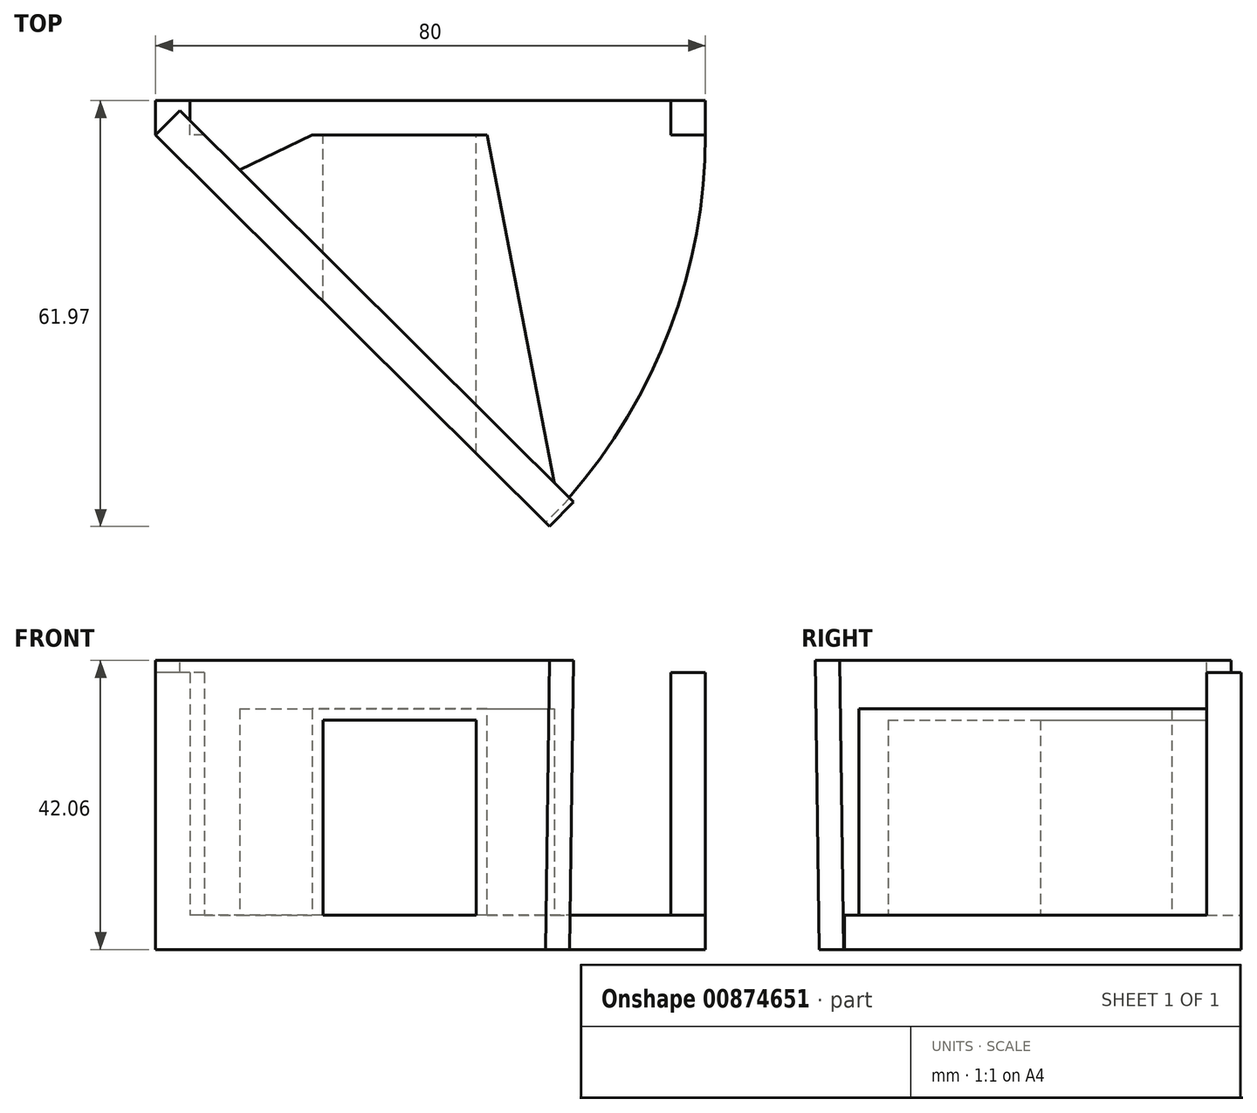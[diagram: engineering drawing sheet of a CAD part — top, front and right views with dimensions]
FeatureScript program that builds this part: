
annotation { "Feature Type Name" : "Feature", "Feature Type Description" : "" }
export const myFeature = defineFeature(function(context is Context, id is Id, definition is map)
    precondition{}
    {
        {
            var Q0;
            Q0=qCreatedBy(makeId("Front.planeOp"),FACE);
            var sketch = newSketch(context, id + "F0", { "sketchPlane" : qUnion([Q0])});
            skLineSegment(sketch, "E0.bottom", {"start": v(0, 0) * mm, "end": v(-80, 0) * mm});
            skLineSegment(sketch, "E0.top", {"start": v(0, 40.27) * mm, "end": v(-80, 40.27) * mm});
            skLineSegment(sketch, "E0.left", {"start": v(0, 0) * mm, "end": v(0, 40.27) * mm});
            skLineSegment(sketch, "E0.right", {"start": v(-80, 0) * mm, "end": v(-80, 40.27) * mm});
            skSolve(sketch);
        }
        {
            var Q0;
            Q0 = qSketchRegion(id + "F0", true);
            extrude(context, id + "F1", {"entities" : qUnion([Q0]), "depth" : 5 * mm, "offsetDistance" : 25 * mm});
        }
        {
            var Q0;
            Q0=qCreatedBy(makeId("Top.planeOp"),FACE);
            var sketch = newSketch(context, id + "F2", { "sketchPlane" : qUnion([Q0])});
            skLineSegment(sketch, "E1", {"start": v(0, -4.77) * mm, "end": v(-80, -5) * mm});
            skArc(sketch, "E2", {"start": v(0, -4.77) * mm, "mid": v(-6, -35.4) * mm, "end": v(-23.27, -61.4) * mm});
            skLineSegment(sketch, "E3", {"start": v(-80, -5) * mm, "end": v(-23.27, -61.4) * mm});
            skSolve(sketch);
        }
        {
            var Q0;
            Q0 = qSketchRegion(id + "F2", true);
            extrude(context, id + "F3", {"entities" : qUnion([Q0]), "operationType" : NewBodyOperationType.ADD, "depth" : 5 * mm, "offsetDistance" : 25 * mm});
        }
        {
            var Q0;
            Q0=makeQuery(id+"F3.opExtrude","SWEPT_FACE",FACE,{"disambiguationData":[OSD([sQuery(id+"F2.wireOp",EDGE,"E3")])]});
            var sketch = newSketch(context, id + "F4", { "sketchPlane" : qUnion([Q0])});
            skLineSegment(sketch, "E4", {"start": v(-53.2, 0) * mm, "end": v(-53.2, 42.06) * mm});
            skLineSegment(sketch, "E5", {"start": v(-53.2, 42.06) * mm, "end": v(27.6, 42.06) * mm});
            skLineSegment(sketch, "E6", {"start": v(27.6, 42.06) * mm, "end": v(26.8, 0) * mm});
            skLineSegment(sketch, "E7", {"start": v(26.8, 0) * mm, "end": v(-53.2, 0) * mm});
            skSolve(sketch);
        }
        {
            var Q0;
            Q0 = qSketchRegion(id + "F4", true);
            extrude(context, id + "F5", {"entities" : qUnion([Q0]), "operationType" : NewBodyOperationType.ADD, "oppositeDirection" : true, "depth" : 5 * mm, "offsetDistance" : 25 * mm});
        }
        {
            var Q0;
            Q0=makeQuery(id+"F3.opExtrude","CAP_FACE",FACE,{"disambiguationData":[OSD([sQuery(id+"F2.wireOp",EDGE,"E1"),sQuery(id+"F2.wireOp",EDGE,"E2"),sQuery(id+"F2.wireOp",EDGE,"E3")])],"isStart":false});
            var sketch = newSketch(context, id + "F6", { "sketchPlane" : qUnion([Q0])});
            skLineSegment(sketch, "E8", {"start": v(-67.78, -10.1) * mm, "end": v(-46.87, 0) * mm});
            skLineSegment(sketch, "E9", {"start": v(-46.87, 0) * mm, "end": v(-32.7, 0) * mm});
            skLineSegment(sketch, "E10", {"start": v(-32.7, 0) * mm, "end": v(-22, -55.62) * mm});
            skLineSegment(sketch, "E11", {"start": v(-22, -55.62) * mm, "end": v(-67.78, -10.1) * mm});
            skSolve(sketch);
        }
        {
            var Q0;
            Q0 = qSketchRegion(id + "F6", true);
            extrude(context, id + "F7", {"entities" : qUnion([Q0]), "operationType" : NewBodyOperationType.ADD, "depth" : 30 * mm, "offsetDistance" : 25 * mm});
        }
        {
            var Q0;
            Q0=makeQuery(id+"F1.opExtrude","CAP_FACE",FACE,{"disambiguationData":[OSD([sQuery(id+"F0.wireOp",EDGE,"E0.bottom"),sQuery(id+"F0.wireOp",EDGE,"E0.top"),sQuery(id+"F0.wireOp",EDGE,"E0.left"),sQuery(id+"F0.wireOp",EDGE,"E0.right")])],"isStart":true});
            var sketch = newSketch(context, id + "F8", { "sketchPlane" : qUnion([Q0])});
            skLineSegment(sketch, "E12.bottom", {"start": v(5, 40.27) * mm, "end": v(75, 40.27) * mm});
            skLineSegment(sketch, "E12.top", {"start": v(5, 5) * mm, "end": v(75, 5) * mm});
            skLineSegment(sketch, "E12.left", {"start": v(5, 40.27) * mm, "end": v(5, 5) * mm});
            skLineSegment(sketch, "E12.right", {"start": v(75, 40.27) * mm, "end": v(75, 5) * mm});
            skSolve(sketch);
        }
        {
            var Q0;
            Q0 = qSketchRegion(id + "F8", true);
            extrude(context, id + "F9", {"entities" : qUnion([Q0]), "operationType" : NewBodyOperationType.REMOVE, "oppositeDirection" : true, "depth" : 5 * mm, "offsetDistance" : 25 * mm});
        }
        {
            var Q0;
            {var subQ1=sQuery(id+"F6.wireOp",EDGE,"E8");var subQ2=sQuery(id+"F8.wireOp",EDGE,"E12.top");Q0=makeQuery(id+"F9.boolean.opBoolean","COPY",FACE,{"disambiguationData":[TD([makeQuery(id+"F7.opExtrude","SWEPT_FACE",FACE,{"disambiguationData":[OSD([subQ1])]})])],"derivedFrom":makeQuery(id+"F9.opExtrude","CAP_FACE",FACE,{"disambiguationData":[OSD([sQuery(id+"F8.wireOp",EDGE,"E12.bottom"),subQ2,sQuery(id+"F8.wireOp",EDGE,"E12.left"),sQuery(id+"F8.wireOp",EDGE,"E12.right")])],"isStart":false})});}
            var sketch = newSketch(context, id + "F10", { "sketchPlane" : qUnion([Q0])});
            skLineSegment(sketch, "E13.bottom", {"start": v(33.34, 33.4) * mm, "end": v(55.61, 33.4) * mm});
            skLineSegment(sketch, "E13.top", {"start": v(33.34, 5) * mm, "end": v(55.61, 5) * mm});
            skLineSegment(sketch, "E13.left", {"start": v(33.34, 33.4) * mm, "end": v(33.34, 5) * mm});
            skLineSegment(sketch, "E13.right", {"start": v(55.61, 33.4) * mm, "end": v(55.61, 5) * mm});
            skSolve(sketch);
        }
        {
            var Q0;
            Q0 = qSketchRegion(id + "F10", true);
            extrude(context, id + "F11", {"entities" : qUnion([Q0]), "operationType" : NewBodyOperationType.REMOVE, "oppositeDirection" : true, "depth" : 49.1 * mm, "offsetDistance" : 25 * mm});
        }
    });
